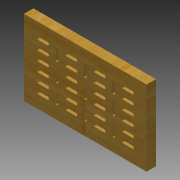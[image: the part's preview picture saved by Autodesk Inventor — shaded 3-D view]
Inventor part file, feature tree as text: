
AUTODESK INVENTOR PART (.ipt)
format: ipt  version: 2014 (Build 180170000, 170)  size: 322,048 bytes
history: native  units: mm
features: extrude x1, sketch x1
ambient origin geometry x8: Origin, YZ Plane, XZ Plane, XY Plane, X Axis, Y Axis, Z Axis, Center Point
bodies: Body1 (feature_tree)
feature tree (2):
  extrude  "Extrusion3"  Depth=80.0mm
  sketch  "Sketch1"  dims[d0=130.0mm d1=80.0mm d5=20.0mm d7=20.0mm d10=20.0mm d14=5.0mm d17=10.0mm d18=3.0mm d28=25.0mm d29=5.0mm d30=10.0mm d32=25.0mm d37=10.0mm d38=3.0mm d40=3.0mm d41=10.0mm d42=10.0mm d44=10.0mm d45=3.0mm d51=15.0mm d52=15.0mm d53=15.0mm d54=15.0mm d55=3.0mm d63=3.0mm d64=3.0mm d65=3.0mm d66=3.0mm d67=3.0mm d68=3.0mm d69=3.0mm d70=3.0mm d71=10.0mm d72=0.0mm]
